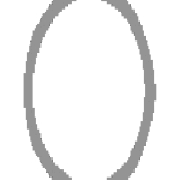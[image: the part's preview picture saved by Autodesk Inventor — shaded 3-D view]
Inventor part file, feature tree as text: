
AUTODESK INVENTOR PART (.ipt)
format: ipt  version: 2021 (Build 250183000, 183)  size: 109,568 bytes
history: native  units: in
note: dims shown in document units (in); Inventor stores cm internally (conversion verified against a paired STEP export)
features: other x4, sketch x3, plane x1
ambient origin geometry x8: Origin, YZ Plane, XZ Plane, XY Plane, X Axis, Y Axis, Z Axis, Center Point
bodies: Solid1 (feature_tree), Body (feature_tree)
feature tree (8):
  other  "Driven Length"
  other  "Frame Generator"
  other  "Start Plane"
  other  "End Plane"
  sketch  "Sketch"  dims[d2=28.1877in d4=-0.0in d5=28.1877in d6=0.12in d7=0.0in d8=90.0deg d9=28.1877in]
  sketch  "Sketch2"  dims[d0=1.0in]
  plane  "Work Plane3"
  sketch  "Sketch3"  dims[d1=0.065in]
